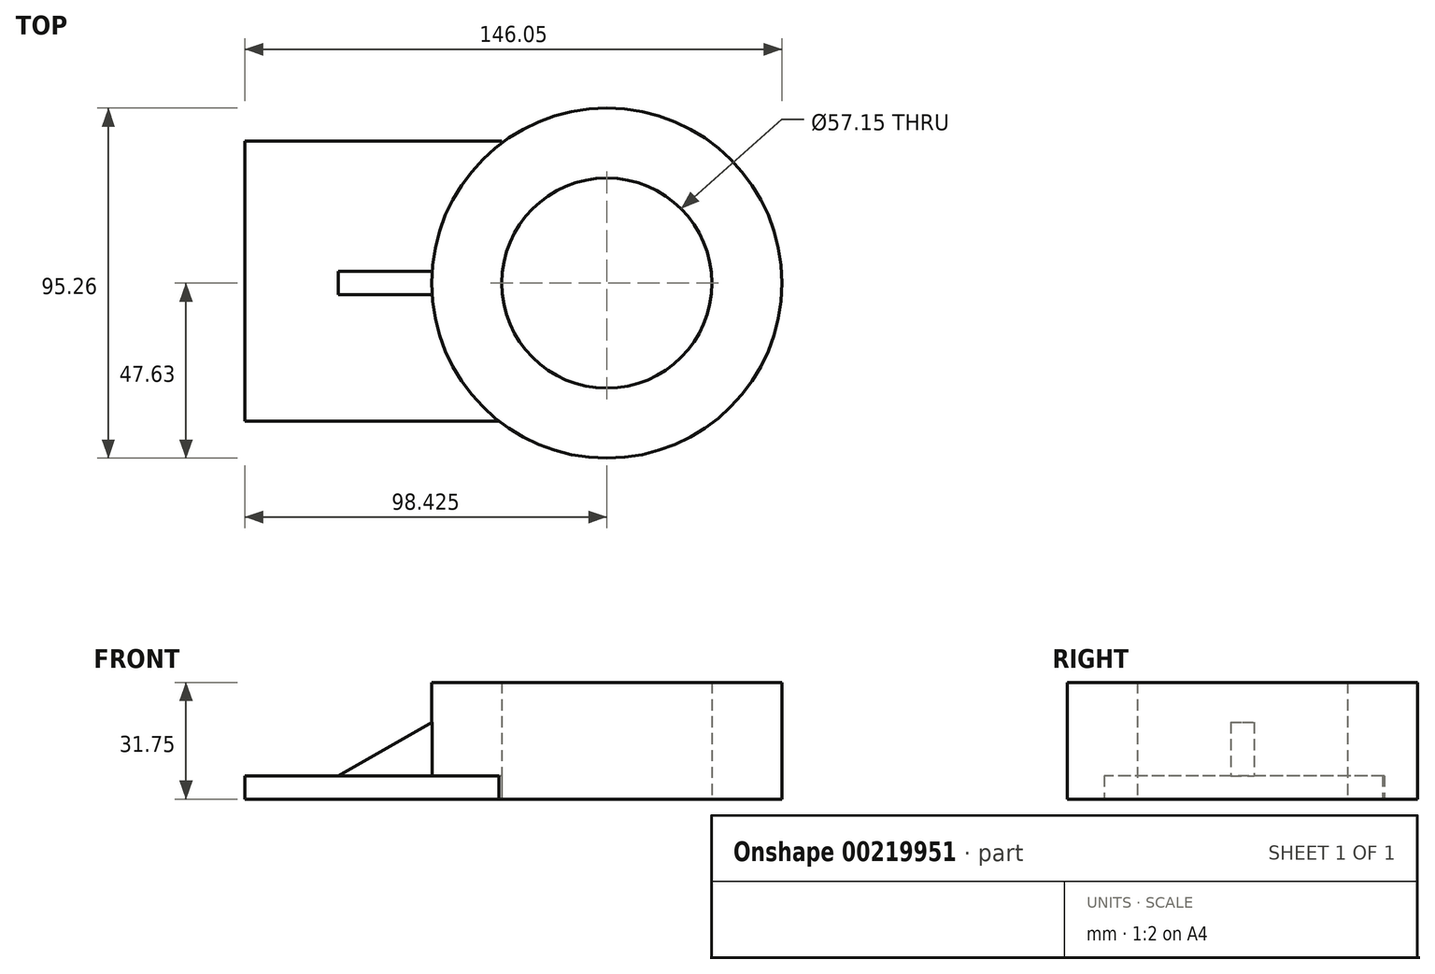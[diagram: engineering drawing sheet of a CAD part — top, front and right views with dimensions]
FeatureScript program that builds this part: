
annotation { "Feature Type Name" : "Feature", "Feature Type Description" : "" }
export const myFeature = defineFeature(function(context is Context, id is Id, definition is map)
    precondition{}
    {
        {
            var Q0;
            Q0=qCreatedBy(makeId("Top.planeOp"),FACE);
            var sketch = newSketch(context, id + "F0", { "sketchPlane" : qUnion([Q0])});
            skLineSegment(sketch, "E0.bottom", {"start": v(0, 38.64) * mm, "end": v(-69.85, 38.64) * mm});
            skLineSegment(sketch, "E0.top", {"start": v(0, -37.56) * mm, "end": v(-69.85, -37.56) * mm});
            skLineSegment(sketch, "E0.left", {"start": v(0, 38.64) * mm, "end": v(0, -37.56) * mm});
            skLineSegment(sketch, "E0.right", {"start": v(-69.85, 38.64) * mm, "end": v(-69.85, -37.56) * mm});
            skSolve(sketch);
        }
        {
            var Q0;
            Q0 = qSketchRegion(id + "F0", true);
            extrude(context, id + "F1", {"entities" : qUnion([Q0]), "depth" : 6.35 * mm});
        }
        {
            var Q0;
            Q0=qCreatedBy(makeId("Front.planeOp"),FACE);
            var sketch = newSketch(context, id + "F2", { "sketchPlane" : qUnion([Q0])});
            skLineSegment(sketch, "E1", {"start": v(0, 6.35) * mm, "end": v(-44.45, 6.35) * mm});
            skLineSegment(sketch, "E2", {"start": v(0, 31.75) * mm, "end": v(0, 6.35) * mm});
            skLineSegment(sketch, "E3", {"start": v(0, 31.75) * mm, "end": v(-44.45, 6.35) * mm});
            skPoint(sketch, "E4.orphan", {"position": v(-69.85, 6.35) * mm});
            skSolve(sketch);
        }
        {
            var Q0;
            Q0 = qSketchRegion(id + "F2", true);
            extrude(context, id + "F3", {"entities" : qUnion([Q0]), "operationType" : NewBodyOperationType.ADD, "endBound" : BoundingType.SYMMETRIC, "depth" : 6.35 * mm});
        }
        {
            var Q0;
            Q0=makeQuery(id+"F1.opExtrude","CAP_FACE",FACE,{"disambiguationData":[OSD([sQuery(id+"F0.wireOp",EDGE,"E0.bottom"),sQuery(id+"F0.wireOp",EDGE,"E0.top"),sQuery(id+"F0.wireOp",EDGE,"E0.left"),sQuery(id+"F0.wireOp",EDGE,"E0.right")])],"isStart":true});
            var sketch = newSketch(context, id + "F4", { "sketchPlane" : qUnion([Q0])});
            skCircle(sketch, "E5", {"center": v(28.58, 0) * mm, "radius": 47.63 * mm});
            skCircle(sketch, "E6.0", {"center": v(28.58, 0) * mm, "radius": 28.58 * mm});
            skSolve(sketch);
        }
        {
            var Q0;
            Q0 = qSketchRegion(id + "F4", true);
            extrude(context, id + "F5", {"entities" : qUnion([Q0]), "operationType" : NewBodyOperationType.ADD, "oppositeDirection" : true, "depth" : 31.75 * mm});
        }
    });
